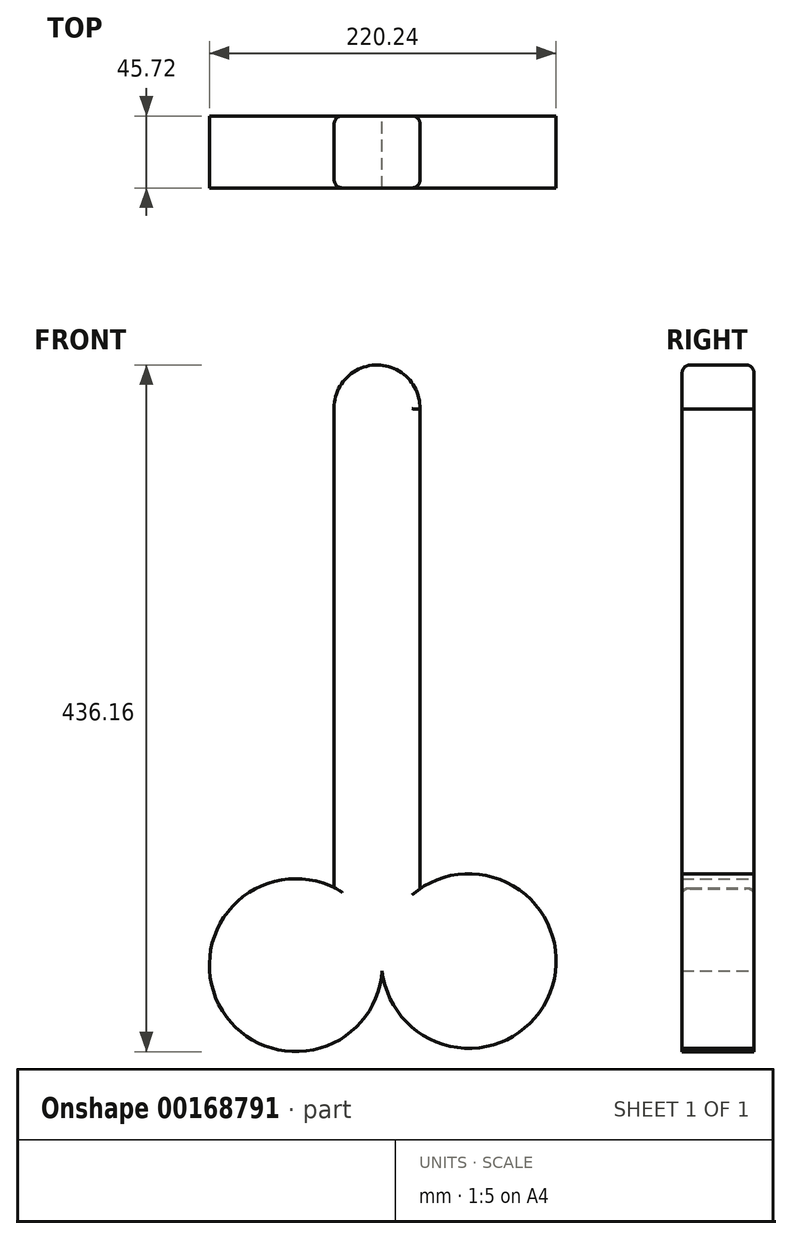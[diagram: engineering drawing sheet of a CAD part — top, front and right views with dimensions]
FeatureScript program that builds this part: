
annotation { "Feature Type Name" : "Feature", "Feature Type Description" : "" }
export const myFeature = defineFeature(function(context is Context, id is Id, definition is map)
    precondition{}
    {
        {
            var Q0;
            Q0=qCreatedBy(makeId("Front.planeOp"),FACE);
            var sketch = newSketch(context, id + "F0", { "sketchPlane" : qUnion([Q0])});
            skLineSegment(sketch, "E0", {"start": v(-23.89, 157.2) * mm, "end": v(-23.89, -147.6) * mm});
            skLineSegment(sketch, "E1", {"start": v(30.62, 156.58) * mm, "end": v(30.62, -148.22) * mm});
            skArc(sketch, "E2", {"start": v(30.62, 156.58) * mm, "mid": v(3.68, 184.45) * mm, "end": v(-23.89, 157.2) * mm});
            skArc(sketch, "E3", {"start": v(6.55, -200.27) * mm, "mid": v(111.97, -217.42) * mm, "end": v(30.62, -148.22) * mm});
            skArc(sketch, "E4", {"start": v(-23.89, -147.6) * mm, "mid": v(-95.78, -224.28) * mm, "end": v(6.55, -200.27) * mm});
            skSolve(sketch);
        }
        {
            var Q0;
            Q0 = qSketchRegion(id + "F0", true);
            extrude(context, id + "F1", {"entities" : qUnion([Q0]), "depth" : 45.72 * mm});
        }
        {
            var Q0;
            Q0=makeQuery(id+"F1.opExtrude","CAP_EDGE",EDGE,{"disambiguationData":[OSD([sQuery(id+"F0.wireOp",EDGE,"E0")])],"isStart":false});
            var Q1;
            Q1=makeQuery(id+"F1.opExtrude","CAP_EDGE",EDGE,{"disambiguationData":[OSD([sQuery(id+"F0.wireOp",EDGE,"E0")])],"isStart":true});
            fillet(context, id + "F2", {"entities" : qUnion([Q0, Q1]), "radius" : 5.08 * mm, "tangentPropagation" : true, "allowEdgeOverflow" : false});
        }
    });
